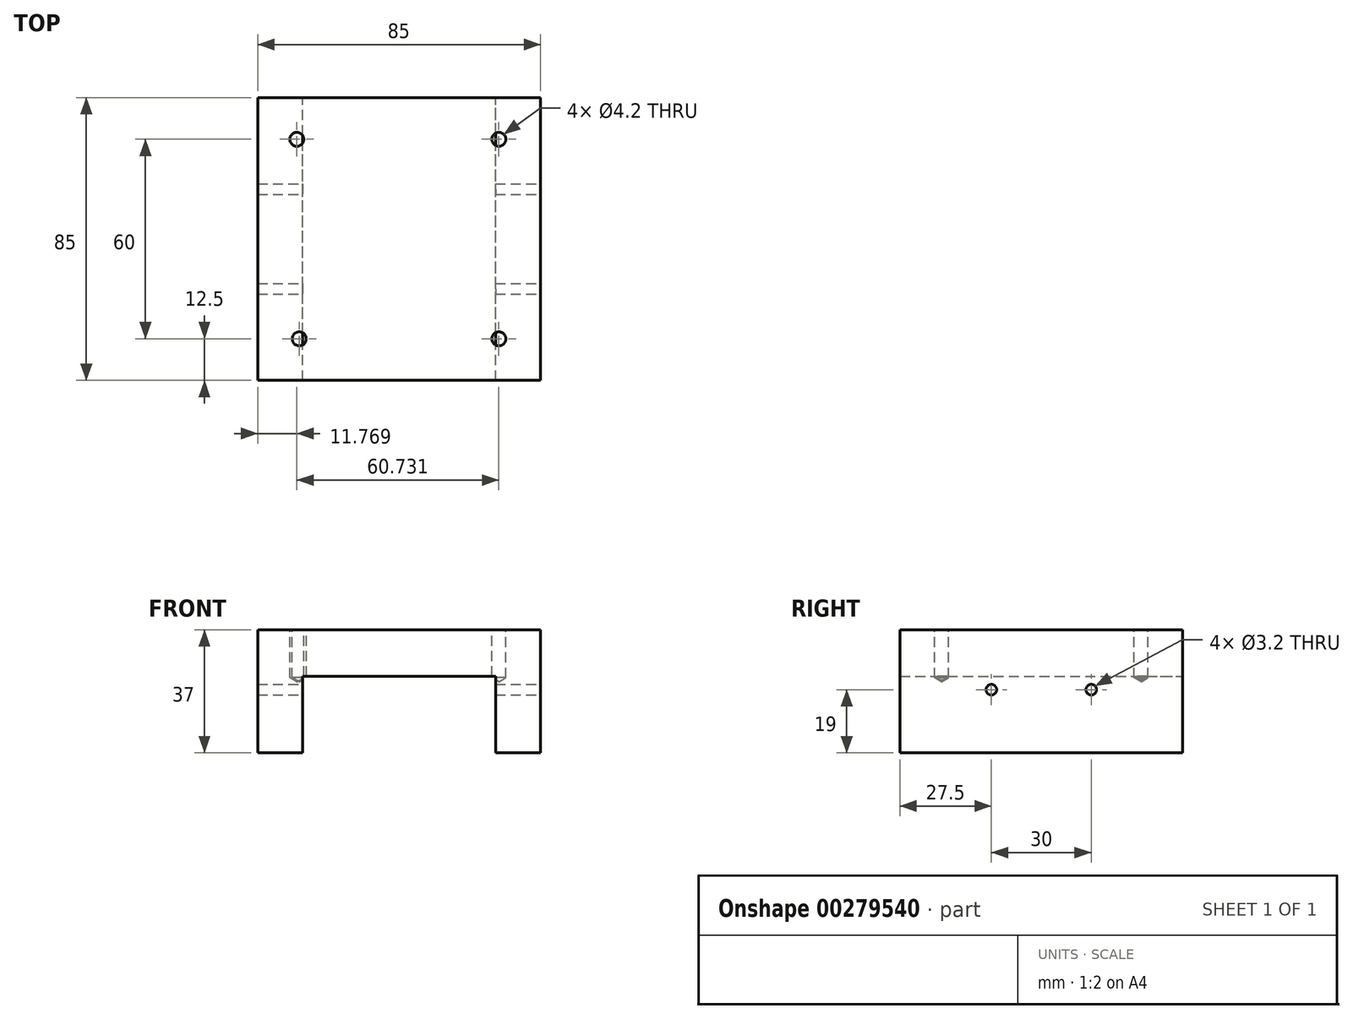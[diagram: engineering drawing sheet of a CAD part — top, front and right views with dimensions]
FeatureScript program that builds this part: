
annotation { "Feature Type Name" : "Feature", "Feature Type Description" : "" }
export const myFeature = defineFeature(function(context is Context, id is Id, definition is map)
    precondition{}
    {
        {
            var Q0;
            Q0=qCreatedBy(makeId("Front.planeOp"),FACE);
            var sketch = newSketch(context, id + "F0", { "sketchPlane" : qUnion([Q0])});
            skLineSegment(sketch, "E0.bottom", {"start": v(0, 0) * mm, "end": v(85, 0) * mm});
            skLineSegment(sketch, "E0.top", {"start": v(0, 37) * mm, "end": v(85, 37) * mm});
            skLineSegment(sketch, "E0.left", {"start": v(0, 0) * mm, "end": v(0, 37) * mm});
            skLineSegment(sketch, "E0.right", {"start": v(85, 0) * mm, "end": v(85, 37) * mm});
            skLineSegment(sketch, "E1.bottom", {"start": v(13.5, 0) * mm, "end": v(71.5, 0) * mm});
            skLineSegment(sketch, "E1.top", {"start": v(13.5, 23) * mm, "end": v(71.5, 23) * mm});
            skLineSegment(sketch, "E1.left", {"start": v(13.5, 0) * mm, "end": v(13.5, 23) * mm});
            skLineSegment(sketch, "E1.right", {"start": v(71.5, 0) * mm, "end": v(71.5, 23) * mm});
            skSolve(sketch);
        }
        {
            var Q0;
            Q0=makeQuery(id+"F0.imprint","IMPRINT",FACE,{"disambiguationData":[TD([[makeQuery(id+"F0.imprint","IMPRINT",EDGE,{"derivedFrom":sQuery(id+"F0.wireOp",EDGE,"E0.top")}),-1.0]])]});
            extrude(context, id + "F1", {"entities" : qUnion([Q0]), "depth" : 85 * mm});
        }
        {
            var Q0;
            Q0=makeQuery(id+"F1.opExtrude","SWEPT_FACE",FACE,{"disambiguationData":[OSD([sQuery(id+"F0.wireOp",EDGE,"E0.top")])]});
            var sketch = newSketch(context, id + "F2", { "sketchPlane" : qUnion([Q0])});
            skPoint(sketch, "E2", {"position": v(11.77, -12.5) * mm});
            skPoint(sketch, "E3", {"position": v(72.5, -12.5) * mm});
            skPoint(sketch, "E4", {"position": v(12.5, -72.5) * mm});
            skPoint(sketch, "E5", {"position": v(72.5, -72.5) * mm});
            skSolve(sketch);
        }
        {
            var Q0;
            Q0=sQuery(id+"F2.wireOp",VERTEX,"E2");
            var Q1;
            Q1=sQuery(id+"F2.wireOp",VERTEX,"E3");
            var Q2;
            Q2=sQuery(id+"F2.wireOp",VERTEX,"E5");
            var Q3;
            Q3=sQuery(id+"F2.wireOp",VERTEX,"E4");
            var Q4;
            Q4=makeQuery(id+"F1.opExtrude","SWEPT_BODY",BODY,{"disambiguationData":[OSD([sQuery(id+"F0.wireOp",EDGE,"E0.bottom"),sQuery(id+"F0.wireOp",EDGE,"E0.top"),sQuery(id+"F0.wireOp",EDGE,"E0.left"),sQuery(id+"F0.wireOp",EDGE,"E0.right"),sQuery(id+"F0.wireOp",EDGE,"E1.top"),sQuery(id+"F0.wireOp",EDGE,"E1.left"),sQuery(id+"F0.wireOp",EDGE,"E1.right")])]});
            hole(context, id + "F3", {"style" : HoleStyle.SIMPLE, "endStyle" : HoleEndStyle.BLIND, "standardTappedOrClearance" : lookupTablePath({ "standard" : "ISO", "engagement" : "75%", "pitch" : "0.8 mm", "size" : "M5", "type" : "Tapped" }), "standardBlindInLast" : lookupTablePath({ "standard" : "ISO", "engagement" : "75%", "pitch" : "0.8 mm", "size" : "M5", "type" : "Tapped" }), "holeDiameter" : 4.2 * mm, "showTappedDepth" : true, "holeDepth" : 14.4 * mm, "tappedDepth" : 12 * mm, "tapClearance" : 3, "locations" : qUnion([Q0, Q1, Q2, Q3]), "scope" : qUnion([Q4]), "majorDiameter" : 5 * mm});
        }
        {
            var Q0;
            Q0=makeQuery(id+"F1.opExtrude","SWEPT_FACE",FACE,{"disambiguationData":[OSD([sQuery(id+"F0.wireOp",EDGE,"E0.right")])]});
            var sketch = newSketch(context, id + "F4", { "sketchPlane" : qUnion([Q0])});
            skPoint(sketch, "E6", {"position": v(-57.5, 19) * mm});
            skPoint(sketch, "E7", {"position": v(-27.5, 19) * mm});
            skSolve(sketch);
        }
        {
            var Q0;
            Q0=sQuery(id+"F4.wireOp",VERTEX,"E6");
            var Q1;
            Q1=sQuery(id+"F4.wireOp",VERTEX,"E7");
            var Q2;
            Q2=makeQuery(id+"F1.opExtrude","SWEPT_BODY",BODY,{"disambiguationData":[OSD([sQuery(id+"F0.wireOp",EDGE,"E0.bottom"),sQuery(id+"F0.wireOp",EDGE,"E0.top"),sQuery(id+"F0.wireOp",EDGE,"E0.left"),sQuery(id+"F0.wireOp",EDGE,"E0.right"),sQuery(id+"F0.wireOp",EDGE,"E1.top"),sQuery(id+"F0.wireOp",EDGE,"E1.left"),sQuery(id+"F0.wireOp",EDGE,"E1.right")])]});
            hole(context, id + "F5", {"style" : HoleStyle.SIMPLE, "endStyle" : HoleEndStyle.THROUGH, "standardTappedOrClearance" : lookupTablePath({ "standard" : "ISO", "engagement" : "75%", "pitch" : "0.75 mm", "size" : "M4", "type" : "Tapped" }), "standardBlindInLast" : lookupTablePath({ "standard" : "ISO", "engagement" : "75%", "pitch" : "0.75 mm", "size" : "M4", "type" : "Tapped" }), "holeDiameter" : 3.2 * mm, "showTappedDepth" : true, "tappedDepth" : 12 * mm, "tapClearance" : 3, "locations" : qUnion([Q0, Q1]), "scope" : qUnion([Q2])});
        }
    });
